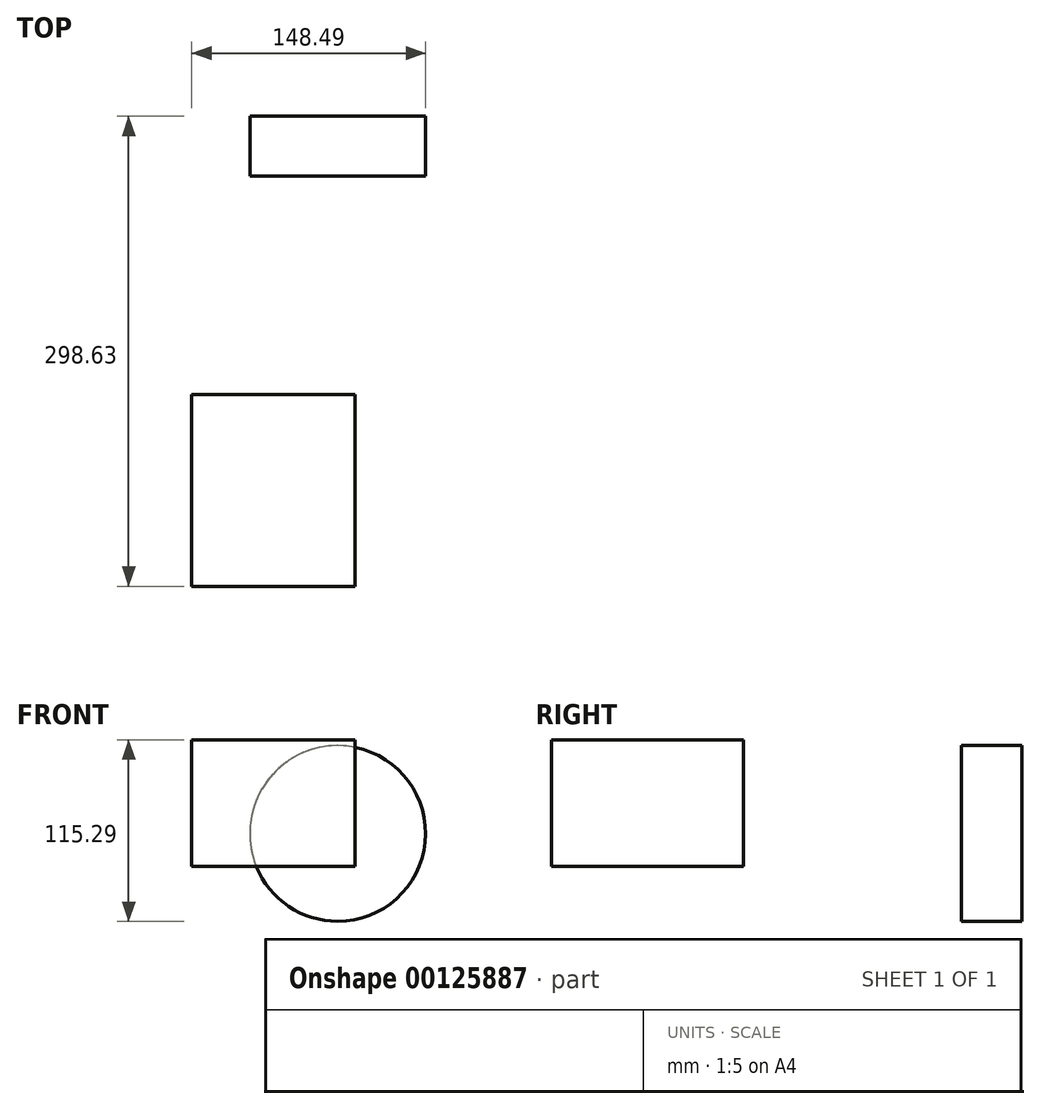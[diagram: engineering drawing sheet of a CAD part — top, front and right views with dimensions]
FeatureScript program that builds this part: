
annotation { "Feature Type Name" : "Feature", "Feature Type Description" : "" }
export const myFeature = defineFeature(function(context is Context, id is Id, definition is map)
    precondition{}
    {
        {
            var Q0;
            Q0=qCreatedBy(makeId("Right.planeOp"),FACE);
            var sketch = newSketch(context, id + "F0", { "sketchPlane" : qUnion([Q0])});
            skLineSegment(sketch, "E0.bottom", {"start": v(-176.7, 119.56) * mm, "end": v(-298.63, 119.56) * mm});
            skLineSegment(sketch, "E0.top", {"start": v(-176.7, 39.18) * mm, "end": v(-298.63, 39.18) * mm});
            skLineSegment(sketch, "E0.left", {"start": v(-176.7, 119.56) * mm, "end": v(-176.7, 39.18) * mm});
            skLineSegment(sketch, "E0.right", {"start": v(-298.63, 119.56) * mm, "end": v(-298.63, 39.18) * mm});
            skSolve(sketch);
        }
        {
            var Q0;
            Q0 = qSketchRegion(id + "F0", true);
            extrude(context, id + "F1", {"entities" : qUnion([Q0]), "depth" : 103.84 * mm});
        }
        {
            var Q0;
            Q0=qCreatedBy(makeId("Front.planeOp"),FACE);
            var sketch = newSketch(context, id + "F2", { "sketchPlane" : qUnion([Q0])});
            skCircle(sketch, "E1", {"center": v(92.69, 60.08) * mm, "radius": 55.8 * mm});
            skSolve(sketch);
        }
        {
            var Q0;
            Q0 = qSketchRegion(id + "F2", true);
            extrude(context, id + "F3", {"entities" : qUnion([Q0]), "depth" : 38.2 * mm});
        }
    });
